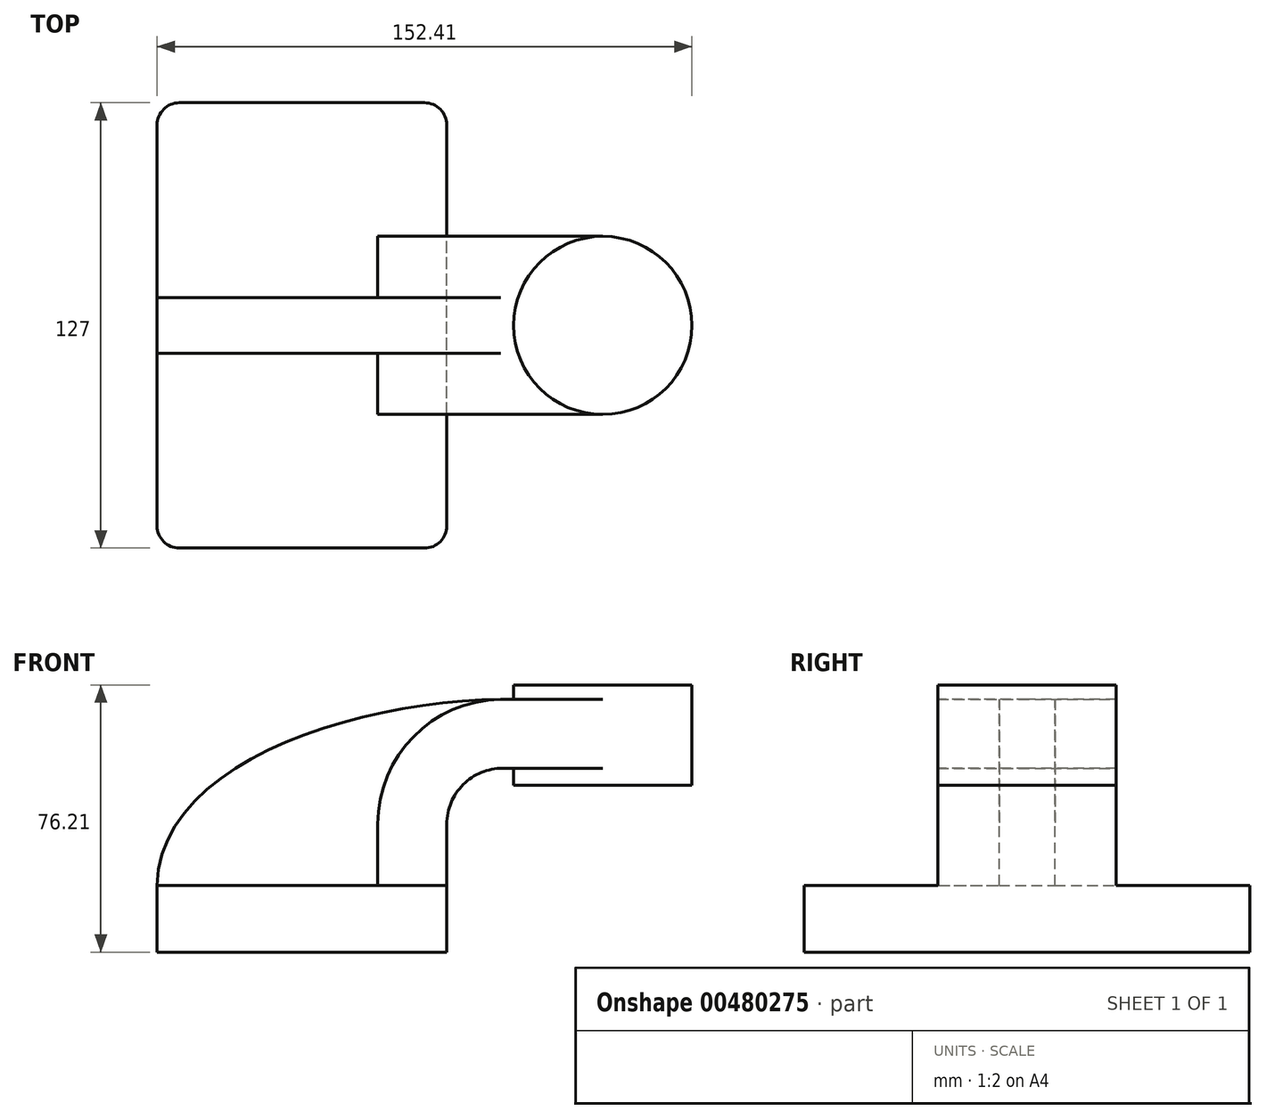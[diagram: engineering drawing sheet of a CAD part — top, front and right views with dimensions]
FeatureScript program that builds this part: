
annotation { "Feature Type Name" : "Feature", "Feature Type Description" : "" }
export const myFeature = defineFeature(function(context is Context, id is Id, definition is map)
    precondition{}
    {
        {
            var Q0;
            Q0=qCreatedBy(makeId("Front.planeOp"),FACE);
            var sketch = newSketch(context, id + "F0", { "sketchPlane" : qUnion([Q0])});
            skLineSegment(sketch, "E0.bottom", {"start": v(41.28, -9.52) * mm, "end": v(-41.28, -9.53) * mm});
            skLineSegment(sketch, "E0.top", {"start": v(41.28, 9.53) * mm, "end": v(-41.28, 9.53) * mm});
            skLineSegment(sketch, "E0.left", {"start": v(41.28, -9.52) * mm, "end": v(41.28, 9.53) * mm});
            skLineSegment(sketch, "E0.right", {"start": v(-41.28, -9.53) * mm, "end": v(-41.28, 9.53) * mm});
            skPoint(sketch, "E0.middle", {"position": v(0, 0) * mm});
            skLineSegment(sketch, "E1.bottom", {"start": v(111.12, 38.1) * mm, "end": v(60.32, 38.1) * mm});
            skLineSegment(sketch, "E1.top", {"start": v(111.12, 66.68) * mm, "end": v(60.32, 66.68) * mm});
            skLineSegment(sketch, "E1.left", {"start": v(111.12, 38.1) * mm, "end": v(111.12, 66.68) * mm});
            skLineSegment(sketch, "E1.right", {"start": v(60.32, 38.1) * mm, "end": v(60.32, 66.67) * mm});
            skPoint(sketch, "E1.middle", {"position": v(85.72, 52.39) * mm});
            skLineSegment(sketch, "E2", {"start": v(41.28, 9.53) * mm, "end": v(41.28, 27) * mm});
            skArc(sketch, "E3", {"start": v(41.27, 27) * mm, "mid": v(45.95, 38.25) * mm, "end": v(57.23, 42.88) * mm});
            skLineSegment(sketch, "E4", {"start": v(57.23, 42.88) * mm, "end": v(85.88, 42.88) * mm});
            skLineSegment(sketch, "E5.0", {"start": v(57.26, 62.56) * mm, "end": v(85.88, 62.56) * mm});
            skArc(sketch, "E5.1", {"start": v(21.59, 27) * mm, "mid": v(32.05, 52.19) * mm, "end": v(57.26, 62.56) * mm});
            skLineSegment(sketch, "E5.2", {"start": v(21.59, 9.53) * mm, "end": v(21.59, 27) * mm});
            skLineSegment(sketch, "E6", {"start": v(85.72, 38.1) * mm, "end": v(85.72, 66.68) * mm});
            skFitSpline(sketch, "E7", {"points": [v(-41.28, 9.53) * mm, v(57.26, 62.56) * mm], "startDerivative": vector(2.2, 106.95) * mm, "endDerivative": vector(120.66, 0.53) * mm});
            skSolve(sketch);
        }
        {
            var Q0;
            Q0=makeQuery(id+"F0.imprint","IMPRINT",FACE,{"disambiguationData":[TD([[makeQuery(id+"F0.imprint","IMPRINT",EDGE,{"derivedFrom":sQuery(id+"F0.wireOp",EDGE,"E0.bottom")}),-1.0]])]});
            extrude(context, id + "F1", {"entities" : qUnion([Q0]), "endBound" : BoundingType.SYMMETRIC, "depth" : 127 * mm});
        }
        {
            var Q0;
            {var subQ0=sQuery(id+"F0.wireOp",EDGE,"E4");var subQ1=sQuery(id+"F0.wireOp",EDGE,"E1.right");var subQ2=makeQuery(id+"F0.imprint","INTERSECT",VERTEX,{"derivedFrom":[subQ1,subQ0]});Q0=makeQuery(id+"F0.imprint","IMPRINT",FACE,{"disambiguationData":[TD([[makeQuery(id+"F0.imprint","IMPRINT",EDGE,{"disambiguationData":[TD([[subQ2,-1.0]])],"derivedFrom":subQ1}),-1.0]])]});}
            var Q1;
            {var subQ1=sQuery(id+"F0.wireOp",EDGE,"E2");Q1=makeQuery(id+"F0.imprint","IMPRINT",FACE,{"disambiguationData":[TD([[makeQuery(id+"F0.imprint","IMPRINT",EDGE,{"derivedFrom":subQ1}),1.0]])]});}
            extrude(context, id + "F2", {"entities" : qUnion([Q0, Q1]), "operationType" : NewBodyOperationType.ADD, "endBound" : BoundingType.SYMMETRIC, "depth" : 50.8 * mm});
        }
        {
            var Q0;
            {var subQ3=sQuery(id+"F0.wireOp",EDGE,"E5.2");Q0=makeQuery(id+"F0.imprint","IMPRINT",FACE,{"disambiguationData":[TD([[makeQuery(id+"F0.imprint","IMPRINT",EDGE,{"derivedFrom":subQ3}),1.0]])]});}
            extrude(context, id + "F3", {"entities" : qUnion([Q0]), "operationType" : NewBodyOperationType.ADD, "endBound" : BoundingType.SYMMETRIC, "depth" : 15.88 * mm});
        }
        {
            var Q0;
            {var subQ0=sQuery(id+"F0.wireOp",EDGE,"E1.left");Q0=makeQuery(id+"F0.imprint","IMPRINT",FACE,{"disambiguationData":[TD([[makeQuery(id+"F0.imprint","IMPRINT",EDGE,{"derivedFrom":subQ0}),1.0]])]});}
            var Q1;
            Q1=sQuery(id+"F0.wireOp",EDGE,"E6");
            revolve(context, id + "F4", {"operationType" : NewBodyOperationType.ADD, "entities" : qUnion([Q0]), "axis" : qUnion([Q1]), "revolveType" : RevolveType.SYMMETRIC, "angle" : 360 * degree});
        }
        {
            var Q0;
            Q0=makeQuery(id+"F1.opExtrude","CAP_EDGE",EDGE,{"disambiguationData":[OSD([sQuery(id+"F0.wireOp",EDGE,"E0.right")])],"isStart":true});
            var Q1;
            Q1=makeQuery(id+"F1.opExtrude","CAP_EDGE",EDGE,{"disambiguationData":[OSD([sQuery(id+"F0.wireOp",EDGE,"E0.right")])],"isStart":false});
            var Q2;
            Q2=makeQuery(id+"F1.opExtrude","CAP_EDGE",EDGE,{"disambiguationData":[OSD([sQuery(id+"F0.wireOp",EDGE,"E0.left")])],"isStart":false});
            var Q3;
            Q3=makeQuery(id+"F1.opExtrude","CAP_EDGE",EDGE,{"disambiguationData":[OSD([sQuery(id+"F0.wireOp",EDGE,"E0.left")])],"isStart":true});
            fillet(context, id + "F5", {"entities" : qUnion([Q0, Q1, Q2, Q3]), "radius" : 6.35 * mm, "tangentPropagation" : true, "allowEdgeOverflow" : false});
        }
    });
